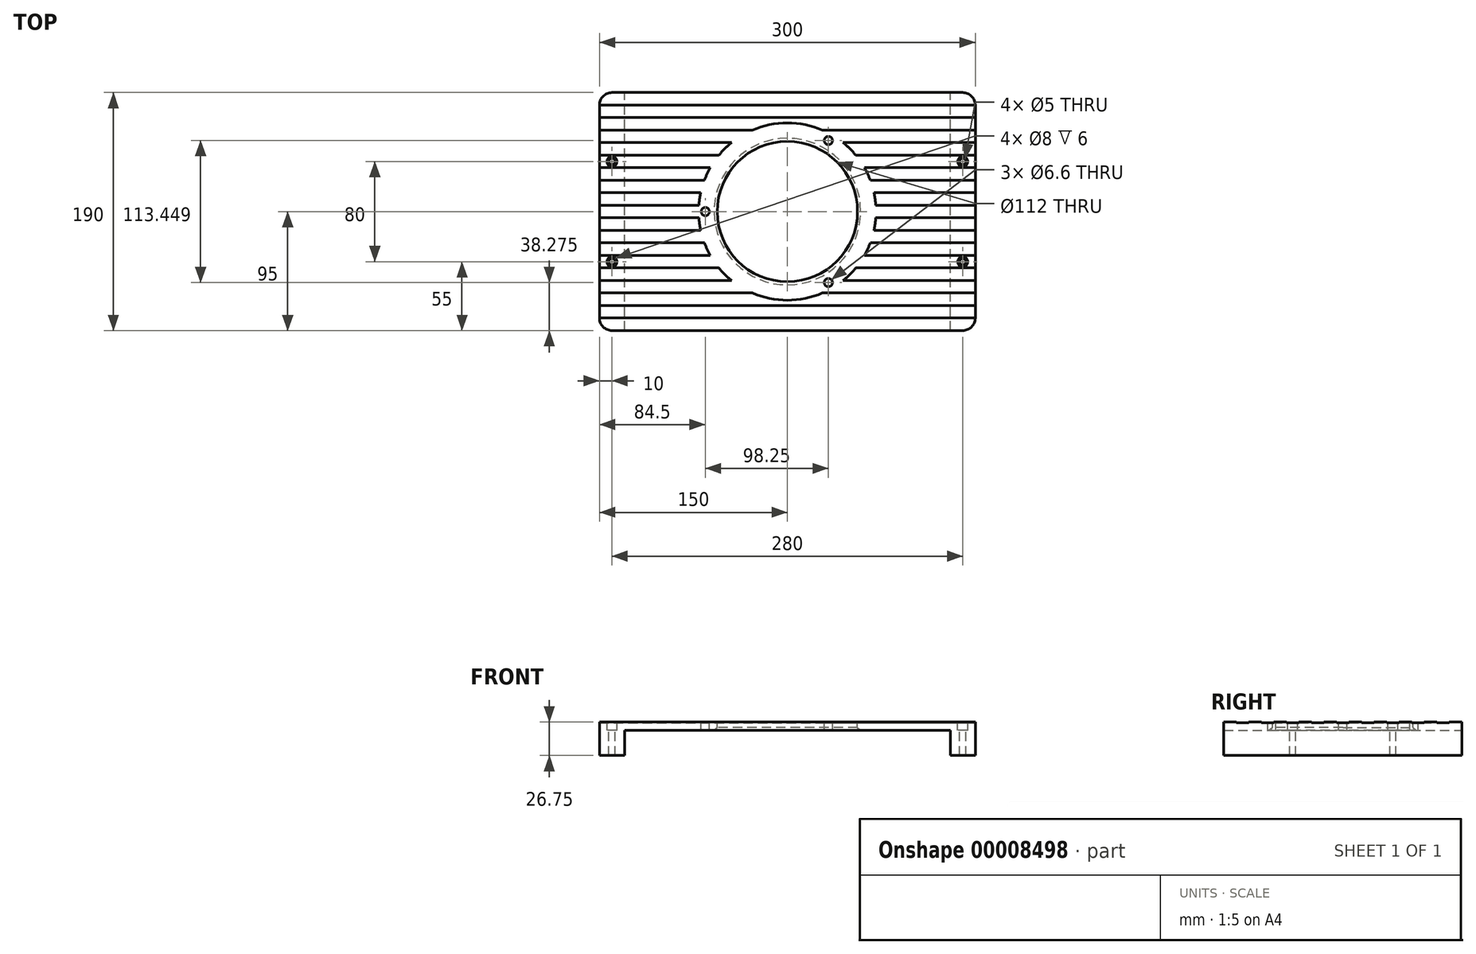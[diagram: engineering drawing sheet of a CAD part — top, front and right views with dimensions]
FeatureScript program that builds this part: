
annotation { "Feature Type Name" : "Feature", "Feature Type Description" : "" }
export const myFeature = defineFeature(function(context is Context, id is Id, definition is map)
    precondition{}
    {
        {
            var Q0;
            Q0=qCreatedBy(makeId("Top.planeOp"),FACE);
            var sketch = newSketch(context, id + "F0", { "sketchPlane" : qUnion([Q0])});
            skLineSegment(sketch, "E0.rect.bottom", {"start": v(150, -95) * mm, "end": v(-150, -95) * mm});
            skLineSegment(sketch, "E0.rect.top", {"start": v(150, 95) * mm, "end": v(-150, 95) * mm});
            skLineSegment(sketch, "E0.rect.left", {"start": v(150, -95) * mm, "end": v(150, 95) * mm});
            skLineSegment(sketch, "E0.rect.right", {"start": v(-150, -95) * mm, "end": v(-150, 95) * mm});
            skPoint(sketch, "E0.rect.middle", {"position": v(0, 0) * mm});
            skSolve(sketch);
        }
        {
            var Q0;
            Q0=makeQuery(id+"F0.imprint","IMPRINT",FACE,{"disambiguationData":[TD([[makeQuery(id+"F0.imprint","IMPRINT",EDGE,{"derivedFrom":sQuery(id+"F0.wireOp",EDGE,"E0.rect.bottom")}),-1.0]])]});
            extrude(context, id + "F1", {"entities" : qUnion([Q0]), "depth" : 26 * mm});
        }
        {
            var Q0;
            Q0=makeQuery(id+"F1.opExtrude","SWEPT_EDGE",EDGE,{"disambiguationData":[OSD([sQuery(id+"F0.wireOp",EDGE,"E0.rect.bottom"),sQuery(id+"F0.wireOp",EDGE,"E0.rect.right")])]});
            var Q1;
            Q1=makeQuery(id+"F1.opExtrude","SWEPT_EDGE",EDGE,{"disambiguationData":[OSD([sQuery(id+"F0.wireOp",EDGE,"E0.rect.bottom"),sQuery(id+"F0.wireOp",EDGE,"E0.rect.left")])]});
            var Q2;
            Q2=makeQuery(id+"F1.opExtrude","SWEPT_EDGE",EDGE,{"disambiguationData":[OSD([sQuery(id+"F0.wireOp",EDGE,"E0.rect.top"),sQuery(id+"F0.wireOp",EDGE,"E0.rect.right")])]});
            var Q3;
            Q3=makeQuery(id+"F1.opExtrude","SWEPT_EDGE",EDGE,{"disambiguationData":[OSD([sQuery(id+"F0.wireOp",EDGE,"E0.rect.top"),sQuery(id+"F0.wireOp",EDGE,"E0.rect.left")])]});
            fillet(context, id + "F2", {"entities" : qUnion([Q0, Q1, Q2, Q3]), "radius" : 10 * mm, "tangentPropagation" : true, "allowEdgeOverflow" : false});
        }
        {
            var Q0;
            Q0=makeQuery(id+"F1.opExtrude","CAP_FACE",FACE,{"disambiguationData":[OSD([sQuery(id+"F0.wireOp",EDGE,"E0.rect.bottom"),sQuery(id+"F0.wireOp",EDGE,"E0.rect.top"),sQuery(id+"F0.wireOp",EDGE,"E0.rect.left"),sQuery(id+"F0.wireOp",EDGE,"E0.rect.right")])],"isStart":true});
            var sketch = newSketch(context, id + "F3", { "sketchPlane" : qUnion([Q0])});
            skLineSegment(sketch, "E1.bottom", {"start": v(130, 95) * mm, "end": v(-130, 95) * mm});
            skLineSegment(sketch, "E1.top", {"start": v(130, -95) * mm, "end": v(-130, -95) * mm});
            skLineSegment(sketch, "E1.left", {"start": v(130, 95) * mm, "end": v(130, -95) * mm});
            skLineSegment(sketch, "E1.right", {"start": v(-130, 95) * mm, "end": v(-130, -95) * mm});
            skSolve(sketch);
        }
        {
            var Q0;
            Q0=makeQuery(id+"F3.imprint","IMPRINT",FACE,{"disambiguationData":[TD([[makeQuery(id+"F3.imprint","IMPRINT",EDGE,{"derivedFrom":sQuery(id+"F3.wireOp",EDGE,"E1.bottom")}),1.0]])]});
            extrude(context, id + "F4", {"entities" : qUnion([Q0]), "operationType" : NewBodyOperationType.REMOVE, "oppositeDirection" : true, "depth" : 20 * mm});
        }
        {
            var Q0;
            Q0=makeQuery(id+"F1.opExtrude","CAP_FACE",FACE,{"disambiguationData":[OSD([sQuery(id+"F0.wireOp",EDGE,"E0.rect.bottom"),sQuery(id+"F0.wireOp",EDGE,"E0.rect.top"),sQuery(id+"F0.wireOp",EDGE,"E0.rect.left"),sQuery(id+"F0.wireOp",EDGE,"E0.rect.right")])],"isStart":false});
            var sketch = newSketch(context, id + "F5", { "sketchPlane" : qUnion([Q0])});
            skCircle(sketch, "E2", {"center": v(0, 0) * mm, "radius": 56 * mm});
            skSolve(sketch);
        }
        {
            var Q0;
            Q0=makeQuery(id+"F5.imprint","IMPRINT",FACE,{"disambiguationData":[TD([[makeQuery(id+"F5.imprint","IMPRINT",EDGE,{"derivedFrom":sQuery(id+"F5.wireOp",EDGE,"E2")}),-1.0]])]});
            extrude(context, id + "F6", {"entities" : qUnion([Q0]), "operationType" : NewBodyOperationType.INTERSECT, "endBound" : BoundingType.THROUGH_ALL, "oppositeDirection" : true, "depth" : 25 * mm});
        }
        {
            var Q0;
            Q0=makeQuery(id+"F1.opExtrude","CAP_FACE",FACE,{"disambiguationData":[OSD([sQuery(id+"F0.wireOp",EDGE,"E0.rect.bottom"),sQuery(id+"F0.wireOp",EDGE,"E0.rect.top"),sQuery(id+"F0.wireOp",EDGE,"E0.rect.left"),sQuery(id+"F0.wireOp",EDGE,"E0.rect.right")])],"isStart":false});
            var sketch = newSketch(context, id + "F7", { "sketchPlane" : qUnion([Q0])});
            skCircle(sketch, "E3", {"center": v(-65.5, 0) * mm, "radius": 3.3 * mm});
            skCircle(sketch, "E4.1.0", {"center": v(32.75, -56.72) * mm, "radius": 3.3 * mm});
            skCircle(sketch, "E4.2.0", {"center": v(32.75, 56.72) * mm, "radius": 3.3 * mm});
            skPoint(sketch, "E4.center", {"position": v(0, 0) * mm});
            skSolve(sketch);
        }
        {
            var Q0;
            Q0=makeQuery(id+"F7.imprint","IMPRINT",FACE,{"disambiguationData":[TD([[makeQuery(id+"F7.imprint","IMPRINT",EDGE,{"derivedFrom":sQuery(id+"F7.wireOp",EDGE,"E3")}),1.0]])]});
            var Q1;
            Q1=makeQuery(id+"F7.imprint","IMPRINT",FACE,{"disambiguationData":[TD([[makeQuery(id+"F7.imprint","IMPRINT",EDGE,{"derivedFrom":sQuery(id+"F7.wireOp",EDGE,"E4.2.0")}),1.0]])]});
            var Q2;
            Q2=makeQuery(id+"F7.imprint","IMPRINT",FACE,{"disambiguationData":[TD([[makeQuery(id+"F7.imprint","IMPRINT",EDGE,{"derivedFrom":sQuery(id+"F7.wireOp",EDGE,"E4.1.0")}),1.0]])]});
            extrude(context, id + "F8", {"entities" : qUnion([Q0, Q1, Q2]), "operationType" : NewBodyOperationType.REMOVE, "endBound" : BoundingType.THROUGH_ALL, "oppositeDirection" : true, "depth" : 25 * mm});
        }
        {
            var Q0;
            Q0=makeQuery(id+"F6.boolean.opBoolean","INTERSECT",EDGE,{"derivedFrom":[makeQuery(id+"F4.boolean.opBoolean","COPY",FACE,{"derivedFrom":makeQuery(id+"F4.opExtrude","CAP_FACE",FACE,{"disambiguationData":[OSD([sQuery(id+"F3.wireOp",EDGE,"E1.bottom"),sQuery(id+"F3.wireOp",EDGE,"E1.top"),sQuery(id+"F3.wireOp",EDGE,"E1.left"),sQuery(id+"F3.wireOp",EDGE,"E1.right")])],"isStart":false})}),makeQuery(id+"F6.opExtrude","SWEPT_FACE",FACE,{"disambiguationData":[OSD([sQuery(id+"F5.wireOp",EDGE,"E2")])]})]});
            chamfer(context, id + "F9", {"entities" : qUnion([Q0]), "width" : 2.5 * mm, "tangentPropagation" : true});
        }
        {
            var Q0;
            Q0=makeQuery(id+"F1.opExtrude","CAP_FACE",FACE,{"disambiguationData":[OSD([sQuery(id+"F0.wireOp",EDGE,"E0.rect.bottom"),sQuery(id+"F0.wireOp",EDGE,"E0.rect.top"),sQuery(id+"F0.wireOp",EDGE,"E0.rect.left"),sQuery(id+"F0.wireOp",EDGE,"E0.rect.right")])],"isStart":false});
            var sketch = newSketch(context, id + "F10", { "sketchPlane" : qUnion([Q0])});
            skCircle(sketch, "E5", {"center": v(140, -40) * mm, "radius": 2.5 * mm});
            skCircle(sketch, "E6.0.1.0", {"center": v(140, 40) * mm, "radius": 2.5 * mm});
            skCircle(sketch, "E6.1.0.0", {"center": v(-140, -40) * mm, "radius": 2.5 * mm});
            skCircle(sketch, "E6.1.1.0", {"center": v(-140, 40) * mm, "radius": 2.5 * mm});
            skLineSegment(sketch, "E6.direction1", {"start": v(140, -40) * mm, "end": v(-140, -40) * mm, "construction": true});
            skLineSegment(sketch, "E6.direction2", {"start": v(140, -40) * mm, "end": v(140, 40) * mm, "construction": true});
            skSolve(sketch);
        }
        {
            var Q0;
            Q0=makeQuery(id+"F10.imprint","IMPRINT",FACE,{"disambiguationData":[TD([[makeQuery(id+"F10.imprint","IMPRINT",EDGE,{"derivedFrom":sQuery(id+"F10.wireOp",EDGE,"E5")}),1.0]])]});
            var Q1;
            Q1=makeQuery(id+"F10.imprint","IMPRINT",FACE,{"disambiguationData":[TD([[makeQuery(id+"F10.imprint","IMPRINT",EDGE,{"derivedFrom":sQuery(id+"F10.wireOp",EDGE,"E6.0.1.0")}),1.0]])]});
            var Q2;
            Q2=makeQuery(id+"F10.imprint","IMPRINT",FACE,{"disambiguationData":[TD([[makeQuery(id+"F10.imprint","IMPRINT",EDGE,{"derivedFrom":sQuery(id+"F10.wireOp",EDGE,"E6.1.0.0")}),1.0]])]});
            var Q3;
            Q3=makeQuery(id+"F10.imprint","IMPRINT",FACE,{"disambiguationData":[TD([[makeQuery(id+"F10.imprint","IMPRINT",EDGE,{"derivedFrom":sQuery(id+"F10.wireOp",EDGE,"E6.1.1.0")}),1.0]])]});
            extrude(context, id + "F11", {"entities" : qUnion([Q0, Q1, Q2, Q3]), "operationType" : NewBodyOperationType.REMOVE, "endBound" : BoundingType.THROUGH_ALL, "oppositeDirection" : true, "depth" : 25 * mm});
        }
        {
            var Q0;
            Q0=makeQuery(id+"F1.opExtrude","CAP_FACE",FACE,{"disambiguationData":[OSD([sQuery(id+"F0.wireOp",EDGE,"E0.rect.bottom"),sQuery(id+"F0.wireOp",EDGE,"E0.rect.top"),sQuery(id+"F0.wireOp",EDGE,"E0.rect.left"),sQuery(id+"F0.wireOp",EDGE,"E0.rect.right")])],"isStart":false});
            var sketch = newSketch(context, id + "F12", { "sketchPlane" : qUnion([Q0])});
            skCircle(sketch, "E7.0", {"center": v(140, -40) * mm, "radius": 4 * mm});
            skArc(sketch, "E8.0", {"start": v(-145, -85) * mm, "mid": v(-143.54, -88.54) * mm, "end": v(-140, -90) * mm});
            skLineSegment(sketch, "E8.1", {"start": v(-145, 85) * mm, "end": v(-145, -85) * mm});
            skArc(sketch, "E8.2", {"start": v(-140, 90) * mm, "mid": v(-143.54, 88.54) * mm, "end": v(-145, 85) * mm});
            skLineSegment(sketch, "E8.3", {"start": v(140, 90) * mm, "end": v(-140, 90) * mm});
            skArc(sketch, "E8.4", {"start": v(145, 85) * mm, "mid": v(143.54, 88.54) * mm, "end": v(140, 90) * mm});
            skLineSegment(sketch, "E8.5", {"start": v(-140, -90) * mm, "end": v(140, -90) * mm});
            skLineSegment(sketch, "E8.6", {"start": v(145, -85) * mm, "end": v(145, 85) * mm});
            skArc(sketch, "E8.7", {"start": v(140, -90) * mm, "mid": v(143.54, -88.54) * mm, "end": v(145, -85) * mm});
            skCircle(sketch, "E9.0.1.0", {"center": v(140, 40) * mm, "radius": 4 * mm});
            skCircle(sketch, "E9.1.0.0", {"center": v(-140, -40) * mm, "radius": 4 * mm});
            skCircle(sketch, "E9.1.1.0", {"center": v(-140, 40) * mm, "radius": 4 * mm});
            skLineSegment(sketch, "E9.direction1", {"start": v(140, -40) * mm, "end": v(-140, -40) * mm, "construction": true});
            skLineSegment(sketch, "E9.direction2", {"start": v(140, -40) * mm, "end": v(140, 40) * mm, "construction": true});
            skSolve(sketch);
        }
        {
            var Q0;
            Q0=makeQuery(id+"F12.imprint","IMPRINT",FACE,{"disambiguationData":[TD([[makeQuery(id+"F12.imprint","IMPRINT",EDGE,{"derivedFrom":sQuery(id+"F12.wireOp",EDGE,"E7.0")}),1.0]])]});
            var Q1;
            Q1=makeQuery(id+"F12.imprint","IMPRINT",FACE,{"disambiguationData":[TD([[makeQuery(id+"F12.imprint","IMPRINT",EDGE,{"derivedFrom":sQuery(id+"F12.wireOp",EDGE,"E9.0.1.0")}),1.0]])]});
            var Q2;
            Q2=makeQuery(id+"F12.imprint","IMPRINT",FACE,{"disambiguationData":[TD([[makeQuery(id+"F12.imprint","IMPRINT",EDGE,{"derivedFrom":sQuery(id+"F12.wireOp",EDGE,"E9.1.0.0")}),1.0]])]});
            var Q3;
            Q3=makeQuery(id+"F12.imprint","IMPRINT",FACE,{"disambiguationData":[TD([[makeQuery(id+"F12.imprint","IMPRINT",EDGE,{"derivedFrom":sQuery(id+"F12.wireOp",EDGE,"E9.1.1.0")}),1.0]])]});
            extrude(context, id + "F13", {"entities" : qUnion([Q0, Q1, Q2, Q3]), "operationType" : NewBodyOperationType.REMOVE, "oppositeDirection" : true, "depth" : 6 * mm});
        }
        {
            var Q0;
            Q0=makeQuery(id+"F1.opExtrude","CAP_FACE",FACE,{"disambiguationData":[OSD([sQuery(id+"F0.wireOp",EDGE,"E0.rect.bottom"),sQuery(id+"F0.wireOp",EDGE,"E0.rect.top"),sQuery(id+"F0.wireOp",EDGE,"E0.rect.left"),sQuery(id+"F0.wireOp",EDGE,"E0.rect.right")])],"isStart":false});
            var sketch = newSketch(context, id + "F14", { "sketchPlane" : qUnion([Q0])});
            skLineSegment(sketch, "E10.bottom", {"start": v(-150, 85) * mm, "end": v(150, 85) * mm});
            skLineSegment(sketch, "E10.top", {"start": v(-150, 75) * mm, "end": v(150, 75) * mm});
            skLineSegment(sketch, "E10.left", {"start": v(-150, 85) * mm, "end": v(-150, 75) * mm});
            skLineSegment(sketch, "E10.right", {"start": v(150, 85) * mm, "end": v(150, 75) * mm});
            skLineSegment(sketch, "E11.0.1.0", {"start": v(-150, 65) * mm, "end": v(-28, 65) * mm});
            skLineSegment(sketch, "E11.0.1.1", {"start": v(-150, 55) * mm, "end": v(-44.54, 55) * mm});
            skLineSegment(sketch, "E11.0.1.2", {"start": v(-150, 65) * mm, "end": v(-150, 55) * mm});
            skLineSegment(sketch, "E11.0.1.3", {"start": v(150, 65) * mm, "end": v(150, 55) * mm});
            skLineSegment(sketch, "E11.0.2.0", {"start": v(-150, 45) * mm, "end": v(-54.62, 45) * mm});
            skLineSegment(sketch, "E11.0.2.1", {"start": v(-150, 35) * mm, "end": v(-61.51, 35) * mm});
            skLineSegment(sketch, "E11.0.2.2", {"start": v(-150, 45) * mm, "end": v(-150, 35) * mm});
            skLineSegment(sketch, "E11.0.2.3", {"start": v(150, 45) * mm, "end": v(150, 35) * mm});
            skLineSegment(sketch, "E11.0.3.0", {"start": v(-150, 25) * mm, "end": v(-66.2, 25) * mm});
            skLineSegment(sketch, "E11.0.3.1", {"start": v(-150, 15) * mm, "end": v(-69.16, 15) * mm});
            skLineSegment(sketch, "E11.0.3.2", {"start": v(-150, 25) * mm, "end": v(-150, 15) * mm});
            skLineSegment(sketch, "E11.0.3.3", {"start": v(150, 25) * mm, "end": v(150, 15) * mm});
            skLineSegment(sketch, "E11.0.4.0", {"start": v(-150, 5) * mm, "end": v(-70.6, 5) * mm});
            skLineSegment(sketch, "E11.0.4.1", {"start": v(-150, -5) * mm, "end": v(-70.6, -5) * mm});
            skLineSegment(sketch, "E11.0.4.2", {"start": v(-150, 5) * mm, "end": v(-150, -5) * mm});
            skLineSegment(sketch, "E11.0.4.3", {"start": v(150, 5) * mm, "end": v(150, -5) * mm});
            skLineSegment(sketch, "E11.0.5.0", {"start": v(-150, -15) * mm, "end": v(-69.16, -15) * mm});
            skLineSegment(sketch, "E11.0.5.1", {"start": v(-150, -25) * mm, "end": v(-66.2, -25) * mm});
            skLineSegment(sketch, "E11.0.5.2", {"start": v(-150, -15) * mm, "end": v(-150, -25) * mm});
            skLineSegment(sketch, "E11.0.5.3", {"start": v(150, -15) * mm, "end": v(150, -25) * mm});
            skLineSegment(sketch, "E11.0.6.0", {"start": v(-150, -35) * mm, "end": v(-61.51, -35) * mm});
            skLineSegment(sketch, "E11.0.6.1", {"start": v(-150, -45) * mm, "end": v(-54.62, -45) * mm});
            skLineSegment(sketch, "E11.0.6.2", {"start": v(-150, -35) * mm, "end": v(-150, -45) * mm});
            skLineSegment(sketch, "E11.0.6.3", {"start": v(150, -35) * mm, "end": v(150, -45) * mm});
            skLineSegment(sketch, "E11.0.7.0", {"start": v(-150, -55) * mm, "end": v(-44.54, -55) * mm});
            skLineSegment(sketch, "E11.0.7.1", {"start": v(-150, -65) * mm, "end": v(-28, -65) * mm});
            skLineSegment(sketch, "E11.0.7.2", {"start": v(-150, -55) * mm, "end": v(-150, -65) * mm});
            skLineSegment(sketch, "E11.0.7.3", {"start": v(150, -55) * mm, "end": v(150, -65) * mm});
            skLineSegment(sketch, "E11.0.8.0", {"start": v(-150, -75) * mm, "end": v(150, -75) * mm});
            skLineSegment(sketch, "E11.0.8.1", {"start": v(-150, -85) * mm, "end": v(150, -85) * mm});
            skLineSegment(sketch, "E11.0.8.2", {"start": v(-150, -75) * mm, "end": v(-150, -85) * mm});
            skLineSegment(sketch, "E11.0.8.3", {"start": v(150, -75) * mm, "end": v(150, -85) * mm});
            skLineSegment(sketch, "E11.direction1", {"start": v(-150, 85) * mm, "end": v(-125, 85) * mm, "construction": true});
            skLineSegment(sketch, "E11.direction2", {"start": v(-150, 85) * mm, "end": v(-150, 65) * mm, "construction": true});
            skArc(sketch, "E12.0", {"start": v(-61.51, 35) * mm, "mid": v(-64.05, 30.1) * mm, "end": v(-66.2, 25) * mm});
            skLineSegment(sketch, "E13.trimOffspring", {"start": v(28, 65) * mm, "end": v(150, 65) * mm});
            skLineSegment(sketch, "E14.trimOffspring", {"start": v(44.54, 55) * mm, "end": v(150, 55) * mm});
            skLineSegment(sketch, "E15.trimOffspring", {"start": v(54.62, 45) * mm, "end": v(150, 45) * mm});
            skLineSegment(sketch, "E16.trimOffspring", {"start": v(61.51, 35) * mm, "end": v(150, 35) * mm});
            skLineSegment(sketch, "E17.trimOffspring", {"start": v(66.2, 25) * mm, "end": v(150, 25) * mm});
            skLineSegment(sketch, "E18.trimOffspring", {"start": v(69.16, 15) * mm, "end": v(150, 15) * mm});
            skLineSegment(sketch, "E19.trimOffspring", {"start": v(70.6, 5) * mm, "end": v(150, 5) * mm});
            skLineSegment(sketch, "E20.trimOffspring", {"start": v(70.6, -5) * mm, "end": v(150, -5) * mm});
            skLineSegment(sketch, "E21.trimOffspring", {"start": v(69.16, -15) * mm, "end": v(150, -15) * mm});
            skLineSegment(sketch, "E22.trimOffspring", {"start": v(66.2, -25) * mm, "end": v(150, -25) * mm});
            skLineSegment(sketch, "E23.trimOffspring", {"start": v(61.51, -35) * mm, "end": v(150, -35) * mm});
            skLineSegment(sketch, "E24.trimOffspring", {"start": v(54.62, -45) * mm, "end": v(150, -45) * mm});
            skLineSegment(sketch, "E25.trimOffspring", {"start": v(44.54, -55) * mm, "end": v(150, -55) * mm});
            skLineSegment(sketch, "E26.trimOffspring", {"start": v(28, -65) * mm, "end": v(150, -65) * mm});
            skArc(sketch, "E27.trimOffspring", {"start": v(-44.54, 55) * mm, "mid": v(-49.83, 50.25) * mm, "end": v(-54.62, 45) * mm});
            skArc(sketch, "E28.trimOffspring", {"start": v(28, 65) * mm, "mid": v(0, 70.77) * mm, "end": v(-28, 65) * mm});
            skArc(sketch, "E29.trimOffspring", {"start": v(54.62, 45) * mm, "mid": v(49.83, 50.25) * mm, "end": v(44.54, 55) * mm});
            skArc(sketch, "E30.trimOffspring", {"start": v(66.2, 25) * mm, "mid": v(64.05, 30.1) * mm, "end": v(61.51, 35) * mm});
            skArc(sketch, "E31.trimOffspring", {"start": v(70.6, 5) * mm, "mid": v(70.06, 10.03) * mm, "end": v(69.16, 15) * mm});
            skArc(sketch, "E32.trimOffspring", {"start": v(69.16, -15) * mm, "mid": v(70.06, -10.03) * mm, "end": v(70.6, -5) * mm});
            skArc(sketch, "E33.trimOffspring", {"start": v(61.51, -35) * mm, "mid": v(64.05, -30.1) * mm, "end": v(66.2, -25) * mm});
            skArc(sketch, "E34.trimOffspring", {"start": v(44.54, -55) * mm, "mid": v(49.83, -50.25) * mm, "end": v(54.62, -45) * mm});
            skArc(sketch, "E35.trimOffspring", {"start": v(-28, -65) * mm, "mid": v(0, -70.77) * mm, "end": v(28, -65) * mm});
            skArc(sketch, "E36.trimOffspring", {"start": v(-54.62, -45) * mm, "mid": v(-49.83, -50.25) * mm, "end": v(-44.54, -55) * mm});
            skArc(sketch, "E37.trimOffspring", {"start": v(-66.2, -25) * mm, "mid": v(-64.05, -30.1) * mm, "end": v(-61.51, -35) * mm});
            skArc(sketch, "E38.trimOffspring", {"start": v(-70.6, -5) * mm, "mid": v(-70.06, -10.03) * mm, "end": v(-69.16, -15) * mm});
            skArc(sketch, "E39.trimOffspring", {"start": v(-69.16, 15) * mm, "mid": v(-70.06, 10.03) * mm, "end": v(-70.6, 5) * mm});
            skSolve(sketch);
        }
        {
            var Q0;
            Q0=makeQuery(id+"F14.imprint","IMPRINT",FACE,{"disambiguationData":[TD([[makeQuery(id+"F14.imprint","IMPRINT",EDGE,{"derivedFrom":sQuery(id+"F14.wireOp",EDGE,"E10.bottom")}),1.0]])]});
            var Q1;
            {var subQ2=sQuery(id+"F14.wireOp",EDGE,"E10.top");Q1=makeQuery(id+"F14.imprint","IMPRINT",FACE,{"disambiguationData":[TD([[makeQuery(id+"F14.imprint","IMPRINT",EDGE,{"derivedFrom":subQ2}),-1.0]])]});}
            var Q2;
            {var subQ2=sQuery(id+"F14.wireOp",EDGE,"E11.0.1.1");Q2=makeQuery(id+"F14.imprint","IMPRINT",FACE,{"disambiguationData":[TD([[makeQuery(id+"F14.imprint","IMPRINT",EDGE,{"derivedFrom":subQ2}),-1.0]])]});}
            var Q3;
            {var subQ2=sQuery(id+"F14.wireOp",EDGE,"E11.0.2.1");Q3=makeQuery(id+"F14.imprint","IMPRINT",FACE,{"disambiguationData":[TD([[makeQuery(id+"F14.imprint","IMPRINT",EDGE,{"derivedFrom":subQ2}),-1.0]])]});}
            var Q4;
            {var subQ2=sQuery(id+"F14.wireOp",EDGE,"E11.0.3.1");Q4=makeQuery(id+"F14.imprint","IMPRINT",FACE,{"disambiguationData":[TD([[makeQuery(id+"F14.imprint","IMPRINT",EDGE,{"derivedFrom":subQ2}),-1.0]])]});}
            var Q5;
            {var subQ2=sQuery(id+"F14.wireOp",EDGE,"E11.0.4.1");Q5=makeQuery(id+"F14.imprint","IMPRINT",FACE,{"disambiguationData":[TD([[makeQuery(id+"F14.imprint","IMPRINT",EDGE,{"derivedFrom":subQ2}),-1.0]])]});}
            var Q6;
            {var subQ2=sQuery(id+"F14.wireOp",EDGE,"E11.0.5.1");Q6=makeQuery(id+"F14.imprint","IMPRINT",FACE,{"disambiguationData":[TD([[makeQuery(id+"F14.imprint","IMPRINT",EDGE,{"derivedFrom":subQ2}),-1.0]])]});}
            var Q7;
            {var subQ2=sQuery(id+"F14.wireOp",EDGE,"E11.0.6.1");Q7=makeQuery(id+"F14.imprint","IMPRINT",FACE,{"disambiguationData":[TD([[makeQuery(id+"F14.imprint","IMPRINT",EDGE,{"derivedFrom":subQ2}),-1.0]])]});}
            var Q8;
            {var subQ2=sQuery(id+"F14.wireOp",EDGE,"E11.0.7.1");Q8=makeQuery(id+"F14.imprint","IMPRINT",FACE,{"disambiguationData":[TD([[makeQuery(id+"F14.imprint","IMPRINT",EDGE,{"derivedFrom":subQ2}),-1.0]])]});}
            var Q9;
            {var subQ2=sQuery(id+"F14.wireOp",EDGE,"E24.trimOffspring");Q9=makeQuery(id+"F14.imprint","IMPRINT",FACE,{"disambiguationData":[TD([[makeQuery(id+"F14.imprint","IMPRINT",EDGE,{"derivedFrom":subQ2}),-1.0]])]});}
            var Q10;
            {var subQ2=sQuery(id+"F14.wireOp",EDGE,"E22.trimOffspring");Q10=makeQuery(id+"F14.imprint","IMPRINT",FACE,{"disambiguationData":[TD([[makeQuery(id+"F14.imprint","IMPRINT",EDGE,{"derivedFrom":subQ2}),-1.0]])]});}
            var Q11;
            {var subQ2=sQuery(id+"F14.wireOp",EDGE,"E20.trimOffspring");Q11=makeQuery(id+"F14.imprint","IMPRINT",FACE,{"disambiguationData":[TD([[makeQuery(id+"F14.imprint","IMPRINT",EDGE,{"derivedFrom":subQ2}),-1.0]])]});}
            var Q12;
            {var subQ2=sQuery(id+"F14.wireOp",EDGE,"E18.trimOffspring");Q12=makeQuery(id+"F14.imprint","IMPRINT",FACE,{"disambiguationData":[TD([[makeQuery(id+"F14.imprint","IMPRINT",EDGE,{"derivedFrom":subQ2}),-1.0]])]});}
            var Q13;
            {var subQ2=sQuery(id+"F14.wireOp",EDGE,"E16.trimOffspring");Q13=makeQuery(id+"F14.imprint","IMPRINT",FACE,{"disambiguationData":[TD([[makeQuery(id+"F14.imprint","IMPRINT",EDGE,{"derivedFrom":subQ2}),-1.0]])]});}
            var Q14;
            {var subQ2=sQuery(id+"F14.wireOp",EDGE,"E14.trimOffspring");Q14=makeQuery(id+"F14.imprint","IMPRINT",FACE,{"disambiguationData":[TD([[makeQuery(id+"F14.imprint","IMPRINT",EDGE,{"derivedFrom":subQ2}),-1.0]])]});}
            var Q15;
            Q15=makeQuery(id+"F14.imprint","IMPRINT",FACE,{"disambiguationData":[TD([[makeQuery(id+"F14.imprint","IMPRINT",EDGE,{"derivedFrom":sQuery(id+"F14.wireOp",EDGE,"E11.0.8.1")}),-1.0]])]});
            extrude(context, id + "F15", {"entities" : qUnion([Q0, Q1, Q2, Q3, Q4, Q5, Q6, Q7, Q8, Q9, Q10, Q11, Q12, Q13, Q14, Q15]), "operationType" : NewBodyOperationType.ADD, "depth" : 0.75 * mm});
        }
    });
